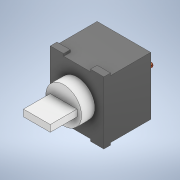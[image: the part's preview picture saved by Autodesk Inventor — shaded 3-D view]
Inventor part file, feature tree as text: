
AUTODESK INVENTOR PART (.ipt)
format: ipt  version: 2020 (Build 240168000, 168)  size: 160,256 bytes
history: native  units: mm
features: extrude x5, sketch x5, fillet x1, projected_geometry x1
ambient origin geometry x8: Origin, YZ Plane, XZ Plane, XY Plane, X Axis, Y Axis, Z Axis, Center Point
bodies: Solid1 (feature_tree)
feature tree (12):
  extrude  "Extrusion1"  Depth=13.0mm
  extrude  "Extrusion2"  Depth=3.0mm
  extrude  "Extrusion3"  Depth=1.5mm TaperAngle=0.0deg
  extrude  "Extrusion4"  Depth=3.0mm TaperAngle=0.0deg
  extrude  "Extrusion5"  Depth=1.5mm
  fillet  "Fillet1"  Radius=6.0mm
  sketch  "Sketch1"  dims[d0=12.0mm d1=13.0mm]
  sketch  "Sketch2"  dims[d2=9.0mm d3=0.0mm d4=3.0mm]
  projected_geometry  "Projected Loop1"
  sketch  "Sketch3"  dims[d5=0.5mm d6=1.5mm d7=0.0mm]
  sketch  "Sketch4"  dims[d8=8.0mm d9=3.0mm d10=0.0mm]
  sketch  "Sketch5"  dims[d11=6.0mm d12=1.5mm d13=6.0mm d14=0.0mm d15=1.0mm d16=1.0mm d17=1.9mm d18=1.9mm d19=3.8mm d20=4.3mm d21=0.0mm d22=0.2mm]
